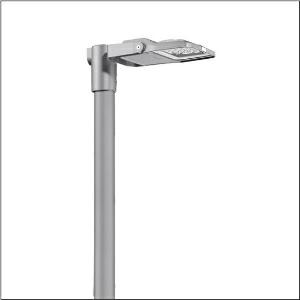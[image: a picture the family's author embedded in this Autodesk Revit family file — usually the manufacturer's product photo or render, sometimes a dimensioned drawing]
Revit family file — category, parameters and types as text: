
# Revit family: floodlight_fl_21_iq_micro___pl52_5xa7761a2d3a_8ecb
name_source: partatom
category: Lighting Fixtures
units: mm (PartAtom-declared; Revit-internal decimal feet)

## family parameters
Cut with Voids When Loaded = No
Host = Face
Light Source = No
Part Type = Normal
Room Calculation Point = No
Round Connector Dimension = Use Diameter
Shared = No

## types (1)
- --- (1 x LED, 2890 lm, 23.1 W, 3000K)
    Apparent Load = 23 VA
    CIE Flux Codes = 26 60 98 100 100
    Color Rendering = 70
    Color Temperature = 3000K
    Default Elevation = 1800 mm
    Description = Floodlight FL 21 iQ micro, floodlight, primary light control with lens, of PMMA, primary optical cover: protective disc, of toughened safety glass, transparent, light distribution: PL52, light emission: direct distribution, installation type: surface-mounted, LED, High Power LED, rated luminous flux: 2.890lm, luminous efficacy: 125lm/W, light colour: 730, colour temperature: 3000K, control: optimised constant luminous flux control (CLO 2.0), Desk-Remote (wireless, voltage-free reading and setting of iQ features in the workshop via application-optimized NFC function/RFID function), Light-Fading, Smart-Wire, Night-Set, Lumen-Switch, Temp-Guard, Auto-Match, with terminal, 6-pole, mains connection: 220..240V, AC, 50/60Hz, start of lifetime: 23W, end of service life: 24W, reduction: 11W, luminaire housing, of diecast aluminium, powder-coated, Siteco® metallic grey (DB 702S), corrosivity category C5 mid according to DIN EN ISO 12944, sealing non-destructively replaceable, please order mast flange separately, mast bracket, of steel, galvanised, powder-coated, Siteco® metallic grey (DB 702S), protection rating (complete): IP66, insulation class (complete): insulation class II (safety insulation), certification: CE, ENEC, VDE, protection symbol: D, impact resistance: IK07, permissible operating ambient temperature: -40..+40°C, permissible operating ambient temperature for outdoor applications: -40..+50°C, standard: DIN EN 12944, LABS conformity tested according to VDMA 24364:2018-05, packaging unit: 1 piece

Light Distribution: PL52
    Height = 65 mm
    Lamp = 1 x LED
    Lamp Light Flux = 2890 lm
    Lamp Power = 23.1 W
    Lamp count = 1
    Length = 312 mm
    Luminous efficacy = 125 lm/W
    Manufacturer = Siteco
    ModVariant = No
    Model = 5XA7761A2D3A
    Number of Poles = 1
    OnlyDefault = Yes
    Power Factor = 1
    Product Name = Floodlight FL 21 iQ micro | PL52
    Product group = floodlight | pylon top
    ProductGroupID = 6101
    Protection Class = Protection class II
    Protection Degree = IP 66
    RLX_Detail_Level = 1
    RLX_Emergency_Light_Flux = 0 lm
    RLX_Emergency_Type = 0
    RLX_Emergency_Type_DB = No
    RlxData = <blob elided: 101929 chars, md5=5ea87474>
    Socket = socket
    Standby Power = 0 W
    System Light Flux = 2890 lm
    System Power = 23 W
    Type Comments = factory setting: luminous flux: 100 % | dim-lin: 254 | 455 mA
    Type Image = l_1007121.jpg
    URL = http://relux.com
    VarID = @adj_129283
    Voltage = 0 V
    Weight = 0.00 kg
    Width = 230 mm

## geometry (parser evidence)
native form markers: Blend x4, Sweep x12
no freeform markers — native parametric forms only
